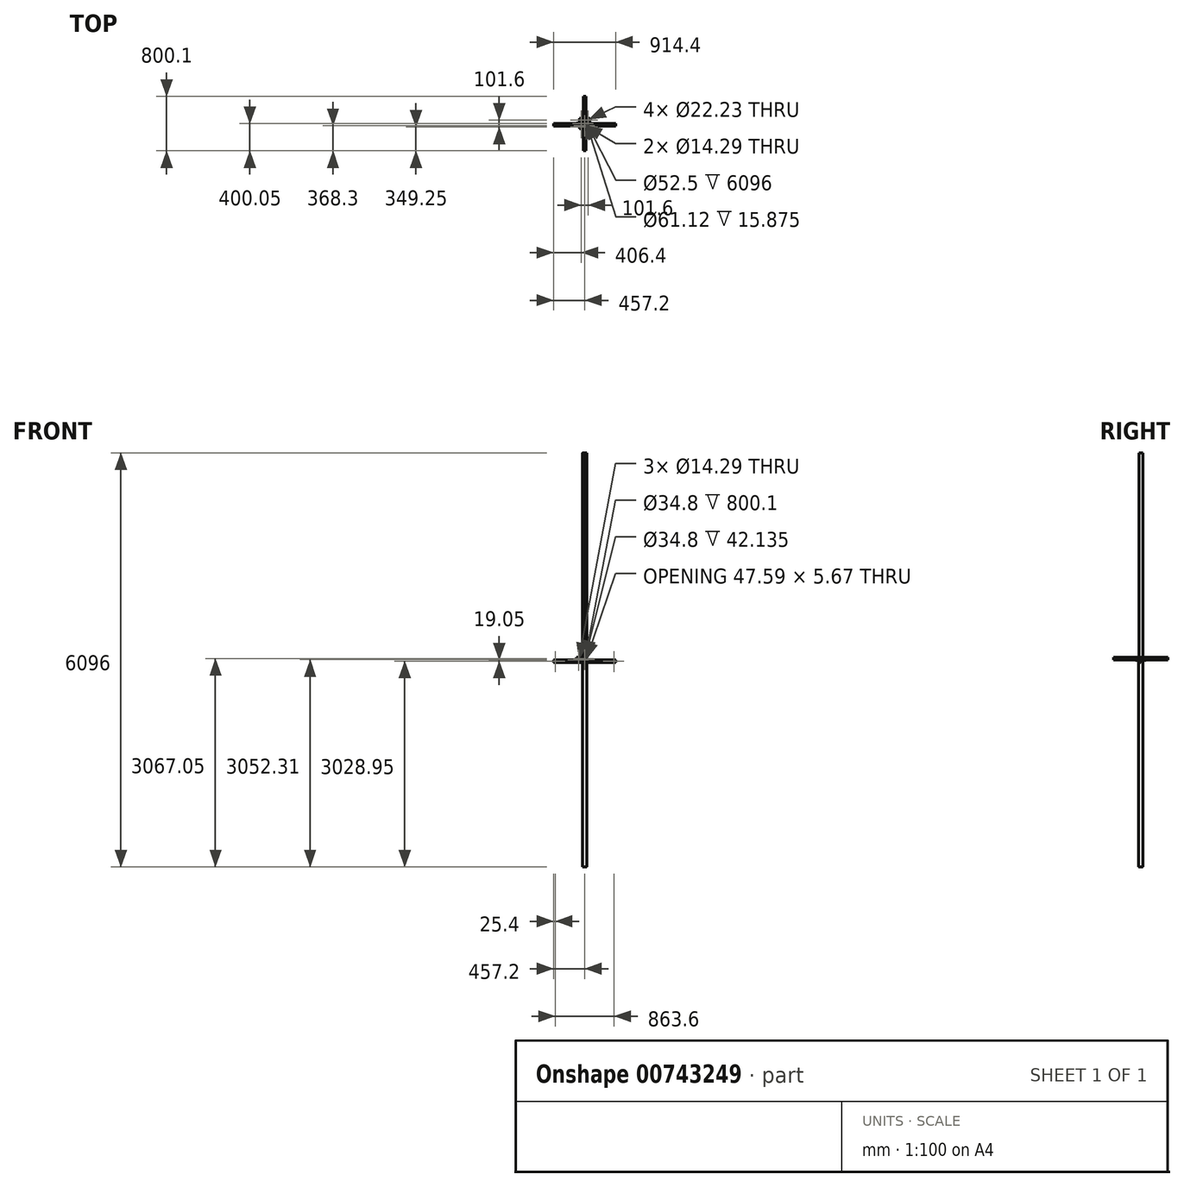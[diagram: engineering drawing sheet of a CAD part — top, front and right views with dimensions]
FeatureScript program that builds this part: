
annotation { "Feature Type Name" : "Feature", "Feature Type Description" : "" }
export const myFeature = defineFeature(function(context is Context, id is Id, definition is map)
    precondition{}
    {
        {
            assignVariable(context, id + "F0", {"name" : "DiagTubeLength", "anyValue" : 44.63 - 2 * 1.25});
        }
        {
            var Q0;
            Q0=qCreatedBy(makeId("Top.planeOp"),FACE);
            var sketch = newSketch(context, id + "F1", { "sketchPlane" : qUnion([Q0])});
            skLineSegment(sketch, "E0.bottom", {"start": v(-76.2, 76.2) * mm, "end": v(76.2, 76.2) * mm});
            skLineSegment(sketch, "E0.top", {"start": v(-76.2, -76.2) * mm, "end": v(76.2, -76.2) * mm});
            skLineSegment(sketch, "E0.left", {"start": v(-76.2, 76.2) * mm, "end": v(-76.2, -76.2) * mm});
            skLineSegment(sketch, "E0.right", {"start": v(76.2, 76.2) * mm, "end": v(76.2, -76.2) * mm});
            skCircle(sketch, "E1", {"center": v(-50.8, 50.8) * mm, "radius": 11.11 * mm});
            skCircle(sketch, "E2.MirrorC", {"center": v(50.8, 50.8) * mm, "radius": 11.11 * mm});
            skCircle(sketch, "E3.MirrorC", {"center": v(-50.8, -50.8) * mm, "radius": 11.11 * mm});
            skCircle(sketch, "E4.MirrorC", {"center": v(50.8, -50.8) * mm, "radius": 11.11 * mm});
            skCircle(sketch, "E5", {"center": v(0, 0) * mm, "radius": 30.56 * mm});
            skSolve(sketch);
        }
        {
            var Q0;
            Q0 = qSketchRegion(id + "F1", true);
            extrude(context, id + "F2", {"entities" : qUnion([Q0]), "endBound" : BoundingType.SYMMETRIC, "depth" : 15.88 * mm, "offsetDistance" : 25.4 * mm});
        }
        {
            var Q0;
            Q0=qCreatedBy(makeId("Front.planeOp"),FACE);
            var sketch = newSketch(context, id + "F3", { "sketchPlane" : qUnion([Q0])});
            skLineSegment(sketch, "E6.bottom", {"start": v(-30.16, -34.93) * mm, "end": v(-120.65, -34.93) * mm});
            skLineSegment(sketch, "E6.top", {"start": v(-30.16, 34.93) * mm, "end": v(-120.65, 34.92) * mm});
            skLineSegment(sketch, "E6.right", {"start": v(-120.65, -34.93) * mm, "end": v(-120.65, 34.92) * mm});
            skCircle(sketch, "E7", {"center": v(-88.9, 0) * mm, "radius": 7.14 * mm});
            skLineSegment(sketch, "E8", {"start": v(-30.16, 34.93) * mm, "end": v(-30.16, -34.93) * mm});
            skPoint(sketch, "E9.orphan", {"position": v(0, -34.92) * mm});
            skSolve(sketch);
        }
        {
            var Q0;
            Q0 = qSketchRegion(id + "F3", true);
            extrude(context, id + "F4", {"entities" : qUnion([Q0]), "endBound" : BoundingType.SYMMETRIC, "depth" : 9.52 * mm, "offsetDistance" : 25.4 * mm});
        }
        {
            var Q0;
            Q0=qCreatedBy(makeId("Top.planeOp"),FACE);
            var sketch = newSketch(context, id + "F5", { "sketchPlane" : qUnion([Q0])});
            skCircle(sketch, "E10", {"center": v(0, 0) * mm, "radius": 30.16 * mm});
            skCircle(sketch, "E11", {"center": v(0, 0) * mm, "radius": 26.25 * mm});
            skSolve(sketch);
        }
        {
            var Q0;
            Q0 = qSketchRegion(id + "F5", true);
            extrude(context, id + "F6", {"entities" : qUnion([Q0]), "endBound" : BoundingType.SYMMETRIC, "depth" : 6096 * mm, "offsetDistance" : 25.4 * mm});
        }
        {
            var Q0;
            Q0=qCreatedBy(makeId("Right.planeOp"),FACE);
            var sketch = newSketch(context, id + "F7", { "sketchPlane" : qUnion([Q0])});
            skLineSegment(sketch, "E12.bottom", {"start": v(-38.1, 0) * mm, "end": v(0, 0) * mm});
            skLineSegment(sketch, "E12.top", {"start": v(-4.76, -38.1) * mm, "end": v(0, -38.1) * mm});
            skLineSegment(sketch, "E12.left", {"start": v(-38.1, 0) * mm, "end": v(-38.1, -4.76) * mm});
            skLineSegment(sketch, "E12.right", {"start": v(0, 0) * mm, "end": v(0, -38.1) * mm});
            skLineSegment(sketch, "E13.top", {"start": v(-38.1, -4.76) * mm, "end": v(-4.76, -4.76) * mm});
            skLineSegment(sketch, "E13.right", {"start": v(-4.76, -38.1) * mm, "end": v(-4.76, -4.76) * mm});
            skSolve(sketch);
        }
        {
            var Q0;
            Q0 = qSketchRegion(id + "F7", true);
            extrude(context, id + "F8", {"entities" : qUnion([Q0]), "endBound" : BoundingType.SYMMETRIC, "depth" : 914.4 * mm, "offsetDistance" : 25.4 * mm});
        }
        {
            var Q0;
            Q0=makeQuery(id+"F8.opExtrude","SWEPT_FACE",FACE,{"disambiguationData":[OSD([sQuery(id+"F7.wireOp",EDGE,"E12.right")])]});
            var sketch = newSketch(context, id + "F9", { "sketchPlane" : qUnion([Q0])});
            skCircle(sketch, "E14", {"center": v(-431.8, -19.05) * mm, "radius": 7.14 * mm});
            skCircle(sketch, "E15.MirrorC", {"center": v(431.8, -19.05) * mm, "radius": 7.14 * mm});
            skSolve(sketch);
        }
        {
            var Q0;
            Q0 = qSketchRegion(id + "F9", true);
            extrude(context, id + "F10", {"entities" : qUnion([Q0]), "operationType" : NewBodyOperationType.REMOVE, "endBound" : BoundingType.THROUGH_ALL, "oppositeDirection" : true, "depth" : 25.4 * mm, "offsetDistance" : 25.4 * mm});
        }
        {
            var Q0;
            Q0=qCreatedBy(makeId("Front.planeOp"),FACE);
            var sketch = newSketch(context, id + "F12", { "sketchPlane" : qUnion([Q0])});
            skLineSegment(sketch, "E16", {"start": v(-20.95, 0) * mm, "end": v(20.95, 0) * mm});
            skArc(sketch, "E17", {"start": v(-16.95, 5.93) * mm, "mid": v(-24.53, 6.74) * mm, "end": v(-20.95, 0) * mm});
            skArc(sketch, "E18.MirrorC", {"start": v(16.95, 5.93) * mm, "mid": v(24.53, 6.74) * mm, "end": v(20.95, 0) * mm});
            skLineSegment(sketch, "E19", {"start": v(-13.41, 3.54) * mm, "end": v(13.41, 3.54) * mm});
            skPoint(sketch, "E20.visualSharp", {"position": v(-16.7, 3.54) * mm});
            skArc(sketch, "E20.filletArc", {"start": v(-16.95, 5.93) * mm, "mid": v(-15.55, 4.2) * mm, "end": v(-13.41, 3.54) * mm});
            skPoint(sketch, "E21.visualSharp", {"position": v(16.7, 3.54) * mm});
            skArc(sketch, "E21.filletArc", {"start": v(13.41, 3.54) * mm, "mid": v(15.55, 4.2) * mm, "end": v(16.95, 5.93) * mm});
            skLineSegment(sketch, "E22.0", {"start": v(-13.41, 2.06) * mm, "end": v(13.41, 2.06) * mm});
            skArc(sketch, "E22.1", {"start": v(18.32, 5.38) * mm, "mid": v(23.31, 5.91) * mm, "end": v(20.95, 1.47) * mm});
            skLineSegment(sketch, "E22.2", {"start": v(-20.95, 1.47) * mm, "end": v(20.95, 1.47) * mm});
            skArc(sketch, "E22.3", {"start": v(13.41, 2.06) * mm, "mid": v(16.37, 2.97) * mm, "end": v(18.32, 5.38) * mm});
            skArc(sketch, "E22.4", {"start": v(-18.32, 5.38) * mm, "mid": v(-23.31, 5.91) * mm, "end": v(-20.95, 1.47) * mm});
            skArc(sketch, "E22.5", {"start": v(-18.32, 5.38) * mm, "mid": v(-16.37, 2.97) * mm, "end": v(-13.41, 2.06) * mm});
            skSolve(sketch);
        }
        {
            var Q0;
            Q0 = qSketchRegion(id + "F12", true);
            extrude(context, id + "F13", {"entities" : qUnion([Q0]), "depth" : 50.8 * mm, "offsetDistance" : 25.4 * mm});
        }
        {
            var Q0;
            Q0=makeQuery(id+"F13.opExtrude","SWEPT_FACE",FACE,{"disambiguationData":[OSD([sQuery(id+"F12.wireOp",EDGE,"E16")])]});
            var sketch = newSketch(context, id + "F14", { "sketchPlane" : qUnion([Q0])});
            skCircle(sketch, "E23", {"center": v(0, 31.75) * mm, "radius": 7.14 * mm});
            skSolve(sketch);
        }
        {
            var Q0;
            Q0 = qSketchRegion(id + "F14", true);
            extrude(context, id + "F15", {"entities" : qUnion([Q0]), "operationType" : NewBodyOperationType.REMOVE, "endBound" : BoundingType.THROUGH_ALL, "oppositeDirection" : true, "depth" : 25.4 * mm, "offsetDistance" : 25.4 * mm});
        }
        {
            var Q0;
            Q0=qCreatedBy(makeId("Front.planeOp"),FACE);
            var sketch = newSketch(context, id + "F16", { "sketchPlane" : qUnion([Q0])});
            skCircle(sketch, "E24", {"center": v(0, 19.05) * mm, "radius": 19.05 * mm});
            skCircle(sketch, "E25", {"center": v(0, 19.05) * mm, "radius": 17.4 * mm});
            skSolve(sketch);
        }
        {
            var Q0;
            Q0 = qSketchRegion(id + "F16", true);
            extrude(context, id + "F17", {"entities" : qUnion([Q0]), "endBound" : BoundingType.SYMMETRIC, "depth" : (getVariable(context, 'DiagTubeLength')) * mm, "offsetDistance" : 25.4 * mm});
        }
        {
            var Q0;
            Q0=qCreatedBy(makeId("Front.planeOp"),FACE);
            var sketch = newSketch(context, id + "F18", { "sketchPlane" : qUnion([Q0])});
            skCircle(sketch, "E26", {"center": v(0, 19.05) * mm, "radius": 19.05 * mm});
            skCircle(sketch, "E27", {"center": v(0, 19.05) * mm, "radius": 17.4 * mm});
            skSolve(sketch);
        }
        {
            var Q0;
            Q0 = qSketchRegion(id + "F18", true);
            extrude(context, id + "F19", {"entities" : qUnion([Q0]), "endBound" : BoundingType.SYMMETRIC, "depth" : 800.1 * mm, "offsetDistance" : 25.4 * mm});
        }
    });
